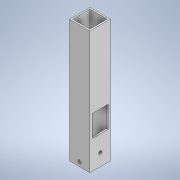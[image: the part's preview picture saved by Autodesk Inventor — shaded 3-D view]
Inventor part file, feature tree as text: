
AUTODESK INVENTOR PART (.ipt)
format: ipt  version: 2022 (Build 260153000, 153)  size: 128,512 bytes
history: native  units: mm
features: extrude x4, sketch x4
ambient origin geometry x8: Origin, YZ Plane, XZ Plane, XY Plane, X Axis, Y Axis, Z Axis, Center Point
bodies: Solid1 (feature_tree)
feature tree (8):
  extrude  "Extrusion1"  Depth=25.4mm
  extrude  "Extrusion2"  Depth=152.4mm TaperAngle=0.0deg
  extrude  "Extrusion3"  Depth=152.4mm TaperAngle=0.0deg
  extrude  "Extrusion4"  TaperAngle=0.0deg  [1 undecoded]
  sketch  "Sketch1"  dims[d0=25.4mm d1=25.4mm]
  sketch  "Sketch2"  dims[d2=2.0mm d3=152.4mm d4=0.0mm]
  sketch  "Sketch3"  dims[d6=4.0mm d7=152.4mm d8=0.0mm]
  sketch  "Sketch4"  dims[d10=4.0mm d11=0.0mm d12=0.0mm d15=10.0mm d16=20.0mm d17=10.0mm d18=0.0mm]
note: 1 required parameter value undecoded (feature->parameter linkage not recoverable at this tier; creation-order binding heuristic only, values carry confidence <= 0.55)
